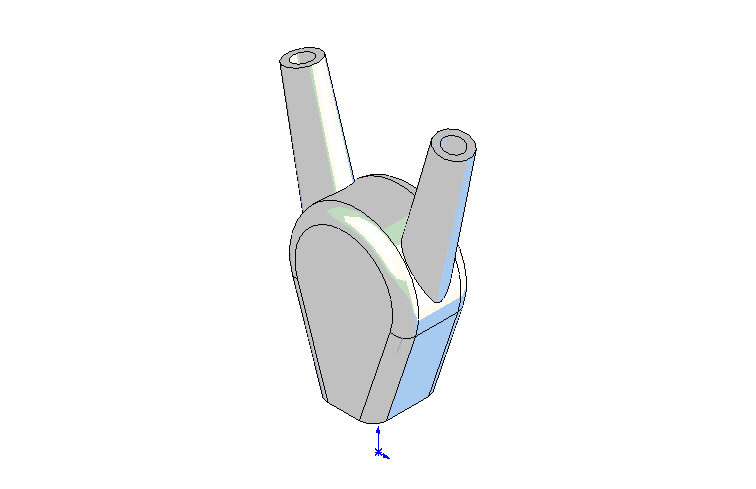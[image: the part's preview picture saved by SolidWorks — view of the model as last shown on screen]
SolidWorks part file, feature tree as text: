
SOLIDWORKS PART (.sldprt)
format: sldprt  version: not decoded by parser v0  size: 260,096 bytes
history: native  units: mm
features: plane x3, sketch x3, material x1, extrude x1, fillet x1, revolve x1, mirror x1, cut_extrude x1 (+10 scaffold rows collapsed)
feature tree (22):
  scaffold x10  (default folders/planes/origin — collapsed)
  material  "Matériau <non spécifié>"
  plane  "Plan de face"
  plane  "Plan de dessus"
  plane  "Plan de droite"
  sketch  "Esquisse1"  dims[c1.D1=~7.967582mm c1.D3=9.5mm c2.D1=26.0mm c2.D2=9.0mm c2.D4=8.0mm]
  extrude  "Extrusion1"  Depth=10.5mm
  fillet  "Congé1"  Radius=2mm
  sketch  "Esquisse3"  dims[c1.D1=~59.772671mm c2.D1=14.0deg c2.D2=6.0mm c2.D3=48.0mm c2.D4=3.0mm c3.D2=5.0mm c3.D5=6.5mm c4.D2=~36.192968mm c5.D2=~179.856352deg c6.D2=3.0mm c6.D3=48.0mm c6.D4=5.0mm c6.D5=6.5mm c6.D6=15.0mm]
  revolve  "Révolution2"  Angle=360deg
  mirror  "Symétrie1"
  sketch  "Esquisse5"  dims[D1=5.0mm D2=6.5mm D3=11.0mm D4=10.0mm]
  cut_extrude  "Enlèv. mat.-Extru.1"  Depth=5mm
decode coverage: 7 of 8 modeling features carry decoded parameters
note: ~ marks probable driven/reference dimensions
note: suppression state not decoded; provenance and decode notes live in map.json
